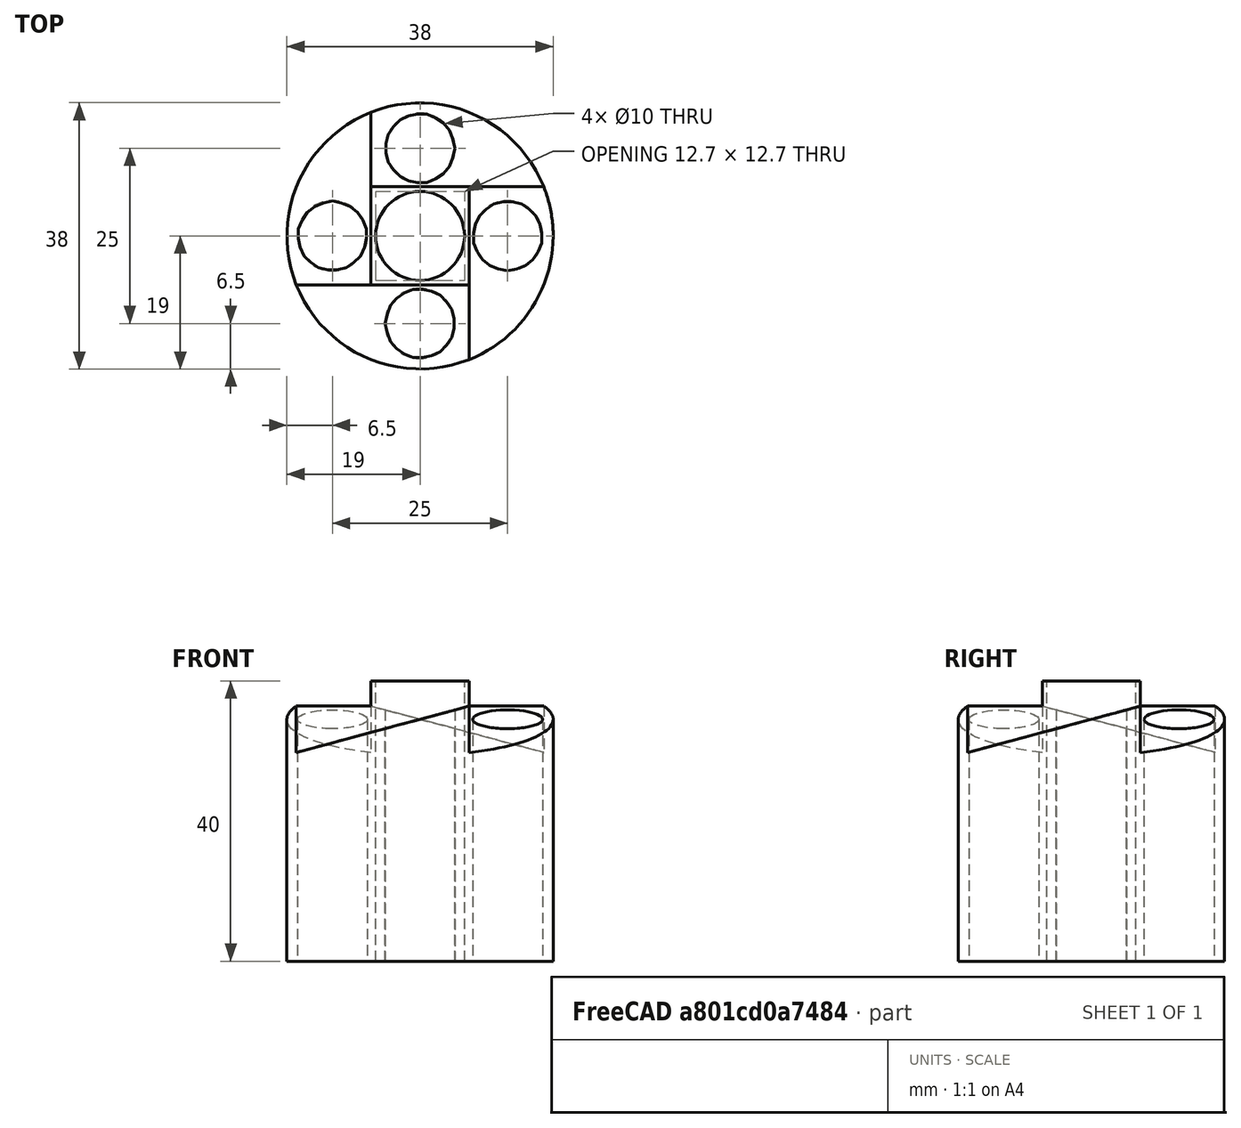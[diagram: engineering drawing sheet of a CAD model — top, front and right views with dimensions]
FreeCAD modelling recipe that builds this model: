
FCSTD DOCUMENT  (FreeCAD 0.20R29410 (Git))
Label: cylinderFour1
License: All rights reserved
LicenseURL: http://en.wikipedia.org/wiki/All_rights_reserved
objects: Part::MultiFuse×11, Part::Cylinder×10, Part::Box×4, Part::Cut×2, Part::Feature×1
note: 28 computed .brp shape members not serialized (recipe doc carries the construction recipe); baked Part::Feature solids carry a one-line shape summary decoded from their .brp

FEATURE [Part::Cylinder] Cylinder
  Angle = 360
  AttacherType = Attacher::AttachEngine3D
  FirstAngle = 0
  Height = 40
  Radius = 19
  SecondAngle = 0
FEATURE [Part::Cylinder] Cylinder001
  Angle = 360
  AttacherType = Attacher::AttachEngine3D
  FirstAngle = 0
  Height = 50
  Placement = pos=(0,12.5,0) rot=(0,0,1;0rad)
  Radius = 5
  SecondAngle = 0
FEATURE [Part::Cylinder] Cylinder003  label="bevilPin"
  Angle = 360
  AttacherType = Attacher::AttachEngine3D
  FirstAngle = 0
  Height = 50
  Radius = 6.35
  SecondAngle = 0
FEATURE [Part::Cylinder] Cylinder004  label="bevilPin001"
  Angle = 360
  AttacherType = Attacher::AttachEngine3D
  FirstAngle = 0
  Height = 50
  Radius = 6.35
  SecondAngle = 0
FEATURE [Part::Box] Box  label="Cube"
  AttacherType = Attacher::AttachEngine3D
  Height = 30
  Length = 40
  Placement = pos=(-19.5582,7,39.7598) rot=(0,1,0;0.261799rad)
  Width = 20
FEATURE [Part::MultiFuse] Fusion
  Shapes = -> [Cylinder001,Box]
FEATURE [Part::MultiFuse] Fusion001
  Shapes = -> [Fusion,Cylinder004]
FEATURE [Part::Box] Box001  label="Cube001"
  AttacherType = Attacher::AttachEngine3D
  Height = 30
  Length = 40
  Placement = pos=(-19.5582,7,39.7598) rot=(0,1,0;0.261799rad)
  Width = 20
FEATURE [Part::Cylinder] Cylinder005
  Angle = 360
  AttacherType = Attacher::AttachEngine3D
  FirstAngle = 0
  Height = 50
  Placement = pos=(0,12.5,0) rot=(0,0,1;0rad)
  Radius = 5
  SecondAngle = 0
FEATURE [Part::Cylinder] Cylinder006  label="bevilPin002"
  Angle = 360
  AttacherType = Attacher::AttachEngine3D
  FirstAngle = 0
  Height = 50
  Radius = 6.35
  SecondAngle = 0
FEATURE [Part::MultiFuse] Fusion002
  Shapes = -> [Cylinder005,Box001]
FEATURE [Part::MultiFuse] Fusion003
  Placement = pos=(0,0,0) rot=(0,0,1;3.14159rad)
  Shapes = -> [Fusion002,Cylinder006]
FEATURE [Part::MultiFuse] Fusion004
  Shapes = -> [Fusion003,Fusion001]
FEATURE [Part::Box] Box002  label="Cube002"
  AttacherType = Attacher::AttachEngine3D
  Height = 30
  Length = 40
  Placement = pos=(-19.5582,7,39.7598) rot=(0,1,0;0.261799rad)
  Width = 20
FEATURE [Part::Box] Box003  label="Cube003"
  AttacherType = Attacher::AttachEngine3D
  Height = 30
  Length = 40
  Placement = pos=(-19.5582,7,39.7598) rot=(0,1,0;0.261799rad)
  Width = 20
FEATURE [Part::Cylinder] Cylinder007
  Angle = 360
  AttacherType = Attacher::AttachEngine3D
  FirstAngle = 0
  Height = 50
  Placement = pos=(0,12.5,0) rot=(0,0,1;0rad)
  Radius = 5
  SecondAngle = 0
FEATURE [Part::Cylinder] Cylinder008  label="bevilPin003"
  Angle = 360
  AttacherType = Attacher::AttachEngine3D
  FirstAngle = 0
  Height = 50
  Radius = 6.35
  SecondAngle = 0
FEATURE [Part::Cylinder] Cylinder009
  Angle = 360
  AttacherType = Attacher::AttachEngine3D
  FirstAngle = 0
  Height = 50
  Placement = pos=(0,12.5,0) rot=(0,0,1;0rad)
  Radius = 5
  SecondAngle = 0
FEATURE [Part::Cylinder] Cylinder010  label="bevilPin004"
  Angle = 360
  AttacherType = Attacher::AttachEngine3D
  FirstAngle = 0
  Height = 50
  Radius = 6.35
  SecondAngle = 0
FEATURE [Part::MultiFuse] Fusion005
  Shapes = -> [Cylinder007,Box002]
FEATURE [Part::MultiFuse] Fusion006
  Shapes = -> [Fusion005,Cylinder008]
FEATURE [Part::MultiFuse] Fusion007
  Shapes = -> [Cylinder009,Box003]
FEATURE [Part::MultiFuse] Fusion008
  Placement = pos=(0,0,0) rot=(0,0,1;3.14159rad)
  Shapes = -> [Fusion007,Cylinder010]
FEATURE [Part::MultiFuse] Fusion009
  Placement = pos=(0,0,0) rot=(0,0,-1;1.5708rad)
  Shapes = -> [Fusion008,Fusion006]
FEATURE [Part::MultiFuse] Fusion010
  Shapes = -> [Fusion009,Fusion004]
FEATURE [Part::Cut] Cut
  Base = -> Cylinder
  Tool = -> Fusion010
FEATURE [Part::Cut] Cut001
  Base = -> Cut
  Tool = -> Cylinder003
FEATURE [Part::Feature] Cut001_solid  label="Cut001 (Solid)"
  shape: bbox 38 x 38 x 40 mm, 19 faces (baked)
